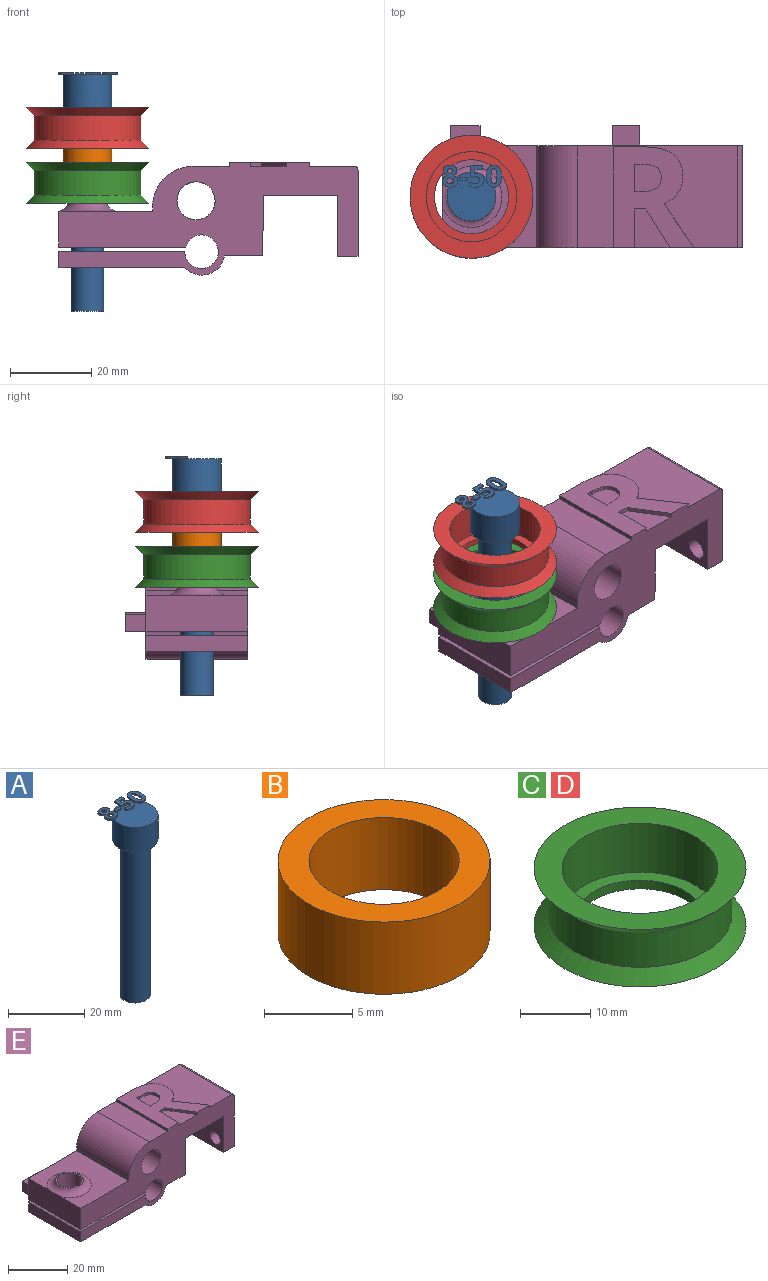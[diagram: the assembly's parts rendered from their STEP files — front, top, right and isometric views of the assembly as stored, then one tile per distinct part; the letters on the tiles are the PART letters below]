
ASSEMBLY  parts=5 mates=4
PART A: 86 faces, bbox 14.5x13.7x58.5 mm
  f0: plane 12x12mm, normal (0,0,1), area 99.4mm2, adj f5,f22,f23,f24,f25,f26,f40,f41
  f1: plane 1x0.26mm, normal (0,0,1), area 0.1mm2, adj f5,f46,f47,f48,f49
  f2: plane 0.85x0.68mm, normal (0,0,1), area 0.2mm2, adj f5,f29,f30,f31
  f3: cylinder r=4mm len=50mm, axis (0,0,-1), area 1256.6mm2, adj f4,f6
  f4: plane 8x8mm, normal (0,0,-1), area 50.3mm2, adj f3
  f5: cylinder r=6mm len=12mm, axis (0,0,-1), area 301.6mm2, adj f0,f1,f2,f6,f39,f45,f67,f85
  f6: plane 12x12mm, normal (0,0,-1), area 62.8mm2, adj f3,f5
  f7: extruded ~0.5x0.46mm, area 0.2mm2, adj f8,f37,f38,f39
  f8: extruded ~0.5x0.46mm, area 0.2mm2, adj f7,f9,f38,f39
  f9: extruded ~0.5x0.39mm, area 0.2mm2, adj f8,f10,f38,f39
  f10: extruded ~0.5x0.4mm, area 0.2mm2, adj f9,f11,f38,f39
  f11: extruded ~0.5x0.49mm, area 0.3mm2, adj f10,f12,f38,f39
  f12: extruded ~0.5x0.5mm, area 0.3mm2, adj f11,f13,f38,f39
  f13: extruded ~0.5x0.39mm, area 0.2mm2, adj f12,f37,f38,f39
  f14: extruded ~1.22x0.5mm, area 0.6mm2, adj f15,f35,f38,f39
  f15: extruded ~1.22x0.5mm, area 0.6mm2, adj f14,f16,f38,f39
  f16: extruded ~0.91x0.5mm, area 0.5mm2, adj f15,f17,f38,f39
  f17: extruded ~0.71x0.5mm, area 0.4mm2, adj f16,f18,f38,f39
  f18: extruded ~0.65x0.61mm, area 0.4mm2, adj f17,f19,f38,f39
  f19: extruded ~0.77x0.62mm, area 0.5mm2, adj f18,f20,f38,f39
  f20: extruded ~0.8x0.5mm, area 0.4mm2, adj f19,f21,f38,f39
  f21: extruded ~1.04x0.5mm, area 0.6mm2, adj f20,f22,f38,f39
  f22: extruded ~1.36x0.5mm, area 0.7mm2, adj f0,f21,f23,f38,f39
  f23: extruded ~1.33x0.5mm, area 0.7mm2, adj f0,f22,f24,f38
  f24: extruded ~1.04x0.51mm, area 0.6mm2, adj f0,f23,f25,f38
  f25: extruded ~0.75x0.5mm, area 0.4mm2, adj f0,f24,f26,f38
  f26: extruded ~0.85x0.66mm, area 0.5mm2, adj f0,f25,f27,f38,f39
  f27: extruded ~0.72x0.56mm, area 0.5mm2, adj f26,f28,f38,f39
  f28: extruded ~0.72x0.5mm, area 0.4mm2, adj f27,f35,f38,f39
  f29: extruded ~0.5x0.45mm, area 0.3mm2, adj f2,f30,f36,f38,f39
  f30: extruded ~0.5x0.47mm, area 0.3mm2, adj f2,f29,f31,f38
  f31: extruded ~0.62x0.5mm, area 0.3mm2, adj f2,f30,f32,f38,f39
  f32: extruded ~0.59x0.5mm, area 0.3mm2, adj f31,f33,f38,f39
  f33: extruded ~0.5x0.48mm, area 0.3mm2, adj f32,f34,f38,f39
  f34: extruded ~0.89x0.77mm, area 0.6mm2, adj f33,f36,f38,f39
  f35: extruded ~0.93x0.5mm, area 0.5mm2, adj f14,f28,f38,f39
  f36: extruded ~0.66x0.5mm, area 0.4mm2, adj f29,f34,f38,f39
  f37: extruded ~0.5x0.39mm, area 0.2mm2, adj f7,f13,f38,f39
  f38: plane 5.4x3.69mm, normal (0,0,1), area 12.7mm2, adj f7,f8,f9,f10,f11,f12,f13,f14
  f39: plane 5.4x3.53mm, normal (0,0,-1), area 10.2mm2, adj f5,f7,f8,f9,f10,f11,f12,f13
  f40: plane 0.9x0.5mm, normal (-1,0,0), area 0.4mm2, adj f0,f41,f43,f44
  f41: plane 1.93x0.5mm, normal (0,-1,0), area 1mm2, adj f0,f40,f42,f44
  f42: plane 0.9x0.5mm, normal (1,0,0), area 0.4mm2, adj f0,f41,f43,f44
  f43: plane 1.93x0.5mm, normal (0,1,0), area 1mm2, adj f0,f40,f42,f44
  f44: plane 1.93x0.9mm, normal (0,0,1), area 1.7mm2, adj f40,f41,f42,f43
  f45: plane 0.76x0.31mm, normal (0,0,-1), area 0mm2, adj f5,f46
  f46: extruded ~1.21x0.5mm, area 0.7mm2, adj f0,f1,f45,f47,f65,f66
  f47: extruded ~0.54x0.5mm, area 0.3mm2, adj f1,f46,f48,f66
  f48: plane 0.5x0.13mm, normal (-0.2,0.98,0), area 0.1mm2, adj f1,f47,f49,f66
  f49: plane 1.03x0.5mm, normal (1,-0.09,0), area 0.5mm2, adj f1,f48,f50,f66,f67
  f50: plane 1.88x0.5mm, normal (0,-1,0), area 0.9mm2, adj f49,f51,f66,f67
  f51: plane 0.94x0.5mm, normal (1,0,0), area 0.5mm2, adj f50,f52,f66,f67
  f52: plane 2.85x0.5mm, normal (0,1,0), area 1.4mm2, adj f51,f53,f66,f67
  f53: plane 2.68x0.5mm, normal (-1,0.07,0), area 1.3mm2, adj f0,f52,f54,f66,f67
  f54: plane 0.5x0.44mm, normal (-0.47,-0.88,0), area 0.3mm2, adj f0,f53,f55,f66
  f55: extruded ~0.5x0.37mm, area 0.2mm2, adj f0,f54,f56,f66
  f56: extruded ~0.5x0.42mm, area 0.2mm2, adj f0,f55,f57,f66
  f57: extruded ~1.05x0.8mm, area 0.8mm2, adj f0,f56,f58,f66
  f58: extruded ~1.02x0.83mm, area 0.8mm2, adj f0,f57,f59,f66
  f59: extruded ~0.72x0.5mm, area 0.4mm2, adj f0,f58,f60,f66
  f60: extruded ~0.66x0.5mm, area 0.4mm2, adj f0,f59,f61,f66
  f61: plane 0.96x0.5mm, normal (-1,0,0), area 0.5mm2, adj f0,f60,f62,f66
  f62: extruded ~1.42x0.5mm, area 0.7mm2, adj f0,f61,f63,f66
  f63: extruded ~1.55x0.5mm, area 0.8mm2, adj f0,f62,f64,f66
  f64: extruded ~1.36x0.54mm, area 0.8mm2, adj f0,f63,f65,f66
  f65: extruded ~1.17x0.5mm, area 0.6mm2, adj f0,f46,f64,f66
  f66: plane 5.33x3.51mm, normal (0,0,1), area 10.9mm2, adj f46,f47,f48,f49,f50,f51,f52,f53
  f67: plane 2.97x1.71mm, normal (0,0,-1), area 3.5mm2, adj f5,f49,f50,f51,f52,f53
  f68: extruded ~1.39x0.5mm, area 0.7mm2, adj f69,f83,f84,f85
  f69: extruded ~1.39x0.5mm, area 0.7mm2, adj f68,f70,f84,f85
  f70: extruded ~0.56x0.5mm, area 0.4mm2, adj f69,f71,f84,f85
  f71: extruded ~0.56x0.5mm, area 0.4mm2, adj f70,f72,f84,f85
  f72: extruded ~1.39x0.5mm, area 0.7mm2, adj f71,f73,f84,f85
  f73: extruded ~1.38x0.5mm, area 0.7mm2, adj f72,f74,f84,f85
  f74: extruded ~0.56x0.5mm, area 0.4mm2, adj f73,f83,f84,f85
  f75: extruded ~2.04x0.5mm, area 1.1mm2, adj f76,f82,f84,f85
  f76: extruded ~2.02x0.5mm, area 1.1mm2, adj f75,f77,f84,f85
  f77: extruded ~1.38x0.69mm, area 0.8mm2, adj f76,f78,f84,f85
  f78: extruded ~1.38x0.66mm, area 0.8mm2, adj f77,f79,f84,f85
  f79: extruded ~2.05x0.5mm, area 1.1mm2, adj f78,f80,f84,f85
  f80: extruded ~2.02x0.5mm, area 1mm2, adj f0,f79,f81,f84,f85
  f81: extruded ~1.37x0.68mm, area 0.8mm2, adj f0,f80,f82,f84
  f82: extruded ~1.39x0.66mm, area 0.8mm2, adj f0,f75,f81,f84,f85
  f83: extruded ~0.56x0.5mm, area 0.4mm2, adj f68,f74,f84,f85
  f84: plane 5.41x3.68mm, normal (0,0,1), area 12.1mm2, adj f68,f69,f70,f71,f72,f73,f74,f75
  f85: plane 5.41x3.68mm, normal (0,0,-1), area 10.3mm2, adj f5,f68,f69,f70,f71,f72,f73,f74
PART B: 4 faces, bbox 12x12x5 mm
  f0: cylinder r=4.25mm len=8.5mm, axis (0,0,-1), area 133.5mm2, adj f2,f3
  f1: cylinder r=6mm len=12mm, axis (0,0,-1), area 188.5mm2, adj f2,f3
  f2: plane 12x12mm, normal (0,0,1), area 56.4mm2, adj f0,f1
  f3: plane 12x12mm, normal (0,0,-1), area 56.4mm2, adj f0,f1
PART C: 8 faces, bbox 30.2x30.2x10 mm
  f0: plane 30.2x30.2mm, normal (0,0,1), area 329.2mm2, adj f1,f7
  f1: cylinder r=11.1mm len=22.2mm, axis (0,0,-1), area 592.8mm2, adj f0,f2
  f2: plane 22.2x22.2mm, normal (0,0,1), area 126.9mm2, adj f1,f3
  f3: cylinder r=9.1mm len=18.2mm, axis (0,0,-1), area 85.8mm2, adj f2,f4
  f4: plane 30.2x30.2mm, normal (0,0,-1), area 456.2mm2, adj f3,f5
  f5: cone r=13.1mm half-angle=45deg, axis (0,0,-1), area 250.6mm2, adj f4,f6
  f6: cylinder r=13.1mm len=26.2mm, axis (0,0,-1), area 493.9mm2, adj f5,f7
  f7: cone r=15.1mm half-angle=45deg, axis (0,0,1), area 250.6mm2, adj f0,f6
PART D: same geometry as C
PART E: 56 faces, bbox 76.9x30x27.7 mm
  f0: plane 39.42x25mm, normal (0,0,1), area 592.1mm2, adj f14,f15,f25,f27,f40,f41,f42,f43
  f1: plane 9.51x8.71mm, normal (0,0,1), area 54.7mm2, adj f14,f37,f38,f39
  f2: plane 25x4.12mm, normal (-1,0,0), area 103mm2, adj f5,f14,f15,f19
  f3: cylinder r=4.17mm len=8.35mm, axis (0,0,1), area 108.1mm2, adj f5,f19
  f4: plane 25x9.34mm, normal (0,0,-1), area 233.4mm2, adj f13,f14,f15,f17
  f5: plane 30.88x25mm, normal (0,0,-1), area 717.2mm2, adj f2,f3,f14,f15,f17
  f6: plane 25x8.82mm, normal (-1,0,0), area 219.6mm2, adj f7,f14,f15,f20,f24
  f7: plane 25x23mm, normal (0,0,1), area 400mm2, adj f6,f8,f14,f15,f24
  f8: plane 25x1.1mm, normal (-1,0,0), area 27.5mm2, adj f7,f14,f15,f25
  f9: plane 25x21.09mm, normal (1,0,0), area 493.5mm2, adj f10,f14,f15,f22,f23,f27
  f10: plane 25x5mm, normal (0,0,-1), area 125mm2, adj f9,f11,f14,f15
  f11: plane 25x15mm, normal (-1,0,0), area 341.3mm2, adj f10,f12,f14,f15,f22,f23
  f12: plane 25x18.2mm, normal (0,0,-1), area 455mm2, adj f11,f13,f14,f15
  f13: plane 25x14.91mm, normal (1,0,-0.01), area 372.8mm2, adj f4,f12,f14,f15
  f14: plane 73.42x27.75mm, normal (0,-1,0), area 1054.6mm2, adj f0,f1,f2,f4,f5,f6,f7,f8
  f15: plane 73.42x26.75mm, normal (0,1,0), area 983.5mm2, adj f0,f2,f4,f5,f6,f7,f8,f9
  f16: cylinder r=4.17mm len=10.78mm, axis (0,0,1), area 282.8mm2, adj f20,f21
  f17: cylinder r=5.75mm len=25mm, axis (0,-1,0), area 315.9mm2, adj f4,f5,f14,f15
  f18: cylinder r=4.1mm len=25mm, axis (0,-1,0), area 618.7mm2, adj f14,f15,f19,f20
  f19: plane 30.91x25mm, normal (0,0,1), area 718.1mm2, adj f2,f3,f14,f15,f18
  f20: plane 31.07x30mm, normal (0,0,-1), area 758.4mm2, adj f6,f14,f15,f16,f18,f29,f30,f31
  f21: plane 9.35x9.35mm, normal (0,0,1), area 13.9mm2, adj f16,f24
  f22: cylinder r=2.43mm len=5mm, axis (1,0,0), area 76.2mm2, adj f9,f11
  f23: cylinder r=2.2mm len=5mm, axis (1,0,0), area 69.1mm2, adj f9,f11
  f24: torus R=7.5mm, axis (0,0,-1), area 134.6mm2, adj f6,f7,f21
  f25: cylinder r=10mm len=25mm, axis (0,-1,0), area 392.7mm2, adj f0,f8,f14,f15
  f26: cylinder r=4.68mm len=25mm, axis (0,-1,0), area 735.2mm2, adj f14,f15
  f27: cylinder r=1mm len=25mm, axis (0,-1,0), area 39.3mm2, adj f0,f9,f14,f15
  f28: plane 7.3x5mm, normal (0,0,1), area 36.5mm2, adj f15,f29,f30,f31
  f29: plane 5x4.12mm, normal (-1,0,0), area 20.6mm2, adj f15,f20,f28,f31
  f30: plane 5x4.12mm, normal (1,0,0), area 20.6mm2, adj f15,f20,f28,f31
  f31: plane 7.3x4.12mm, normal (0,1,0), area 30.1mm2, adj f20,f28,f29,f30
  f32: plane 6.63x5mm, normal (0,0,1), area 33.2mm2, adj f15,f33,f35,f36
  f33: plane 5x4.5mm, normal (-1,0,0), area 22.5mm2, adj f15,f32,f34,f36
  f34: plane 6.63x5mm, normal (0,0,-1), area 33.2mm2, adj f15,f33,f35,f36
  f35: plane 5x4.5mm, normal (1,0,0), area 22.5mm2, adj f15,f32,f34,f36
  f36: plane 6.63x4.5mm, normal (0,1,0), area 29.9mm2, adj f32,f33,f34,f35
  f37: plane 9.51x1mm, normal (1,0,0), area 9.5mm2, adj f1,f14,f38,f54
  f38: plane 2.79x1mm, normal (0,-1,0), area 2.8mm2, adj f1,f37,f39,f54
  f39: plane 9.51x5.92mm, normal (-0.85,-0.53,0), area 11.2mm2, adj f1,f14,f38,f54
  f40: extruded ~10.8x7.29mm, area 13mm2, adj f0,f14,f41,f54
  f41: extruded ~3.41x2.67mm, area 4.4mm2, adj f0,f40,f42,f54
  f42: extruded ~3.89x1.2mm, area 4.1mm2, adj f0,f41,f43,f54
  f43: extruded ~5.59x2.42mm, area 6.3mm2, adj f0,f42,f44,f54
  f44: extruded ~7.48x1.84mm, area 7.8mm2, adj f0,f43,f45,f54
  f45: plane 7.22x1mm, normal (0,1,0), area 7.2mm2, adj f0,f44,f46,f54
  f46: plane 24.79x1mm, normal (-1,0,0), area 24.8mm2, adj f0,f14,f45,f54
  f47: plane 1.69x1mm, normal (0,1,0), area 1.7mm2, adj f48,f53,f54,f55
  f48: plane 6.7x1mm, normal (1,0,0), area 6.7mm2, adj f47,f49,f54,f55
  f49: plane 1.6x1mm, normal (0,-1,0), area 1.6mm2, adj f48,f50,f54,f55
  f50: extruded ~3.75x1mm, area 3.9mm2, adj f49,f51,f54,f55
  f51: extruded ~2.51x1.21mm, area 2.9mm2, adj f50,f52,f54,f55
  f52: extruded ~2.61x1.19mm, area 3mm2, adj f51,f53,f54,f55
  f53: extruded ~3.68x1mm, area 3.8mm2, adj f47,f52,f54,f55
  f54: plane 24.79x19.8mm, normal (0,0,1), area 300mm2, adj f14,f37,f38,f39,f40,f41,f42,f43
  f55: plane 6.7x6.56mm, normal (0,0,1), area 38.8mm2, adj f47,f48,f49,f50,f51,f52,f53
PLACE A t=(-103.78,-12.5,-13.6)mm
PLACE B rot(axis=(1,0,0),180deg) t=(-103.78,-12.5,26.4)mm
PLACE C t=(-103.78,-12.5,18.1)mm
PLACE D t=(-103.78,-12.5,31.6)mm
PLACE E at identity
MATE fastened A.f3 <-> D.f1  axis (0,0,-1) through (-103.78,-12.5,36.4)mm
MATE fastened B.f0 <-> C.f1  axis (0,0,1) through (-103.78,-12.5,21.4)mm
MATE fastened C.f1 <-> E.f3  axis (0,0,-1) through (-103.78,-12.5,12.9)mm
MATE fastened D.f1 <-> B.f0  axis (0,0,-1) through (-103.78,-12.5,26.4)mm
